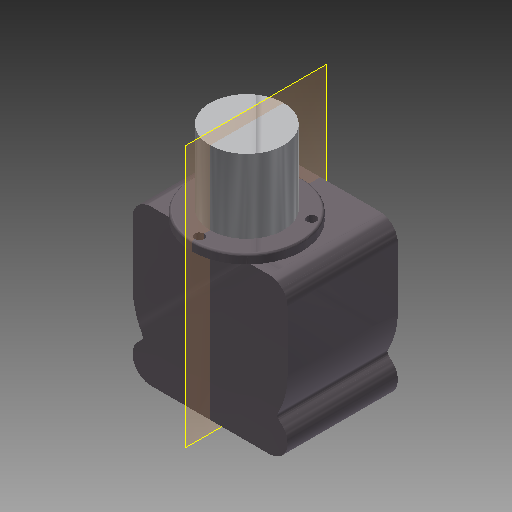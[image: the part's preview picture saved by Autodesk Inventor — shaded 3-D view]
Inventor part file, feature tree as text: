
AUTODESK INVENTOR PART (.ipt)
format: ipt  version: 2017 (Build 210142000, 142)  size: 190,976 bytes
history: native  units: in
note: dims shown in document units (in); Inventor stores cm internally (conversion verified against a paired STEP export)
features: sketch x5, extrude x4, fillet x3, reference x3, projected_geometry x2, hole x1
ambient origin geometry x8: Origin, YZ Plane, XZ Plane, XY Plane, X Axis, Y Axis, Z Axis, Center Point
bodies: Solid1 (feature_tree)
feature tree (18):
  extrude  "Extrusion1"  Depth=2.11in
  fillet  "Fillet1"  Radius=1.5in
  extrude  "Extrusion2"  Depth=0.5in
  fillet  "Fillet2"  Radius=0.5in
  extrude  "Extrusion3"  Depth=1.055in
  fillet  "Fillet3"  Radius=1.0in
  extrude  "Extrusion4"  Depth=1.5in
  hole  "Hole1"  [1 undecoded]
  sketch  "Sketch1"  dims[d0=2.11in d1=2.11in d2=1.5in d3=0.0in]
  sketch  "Sketch3"  dims[d4=0.25in d8=2.0in d9=0.5in]
  sketch  "Sketch4"  dims[d10=0.5in d12=1.055in d13=1.0in d14=0.0in]
  projected_geometry  "Projected Loop1"
  projected_geometry  "Projected Loop2"
  sketch  "Sketch5"  dims[d15=0.0625in d16=1.5in]
  sketch  "Sketch6"  dims[d17=0.25in d18=0.125in d19=0.0in d20=0.0312in d22=1.0in d23=0.0in d24=0.25in d25=0.129in d26=0.75in d27=0.225in d28=0.25in d29=0.5635in d30=0.25in d31=0.8108in]
  reference  "Reference1"
  reference  "Reference2"
  reference  "Reference3"
note: 1 required parameter value undecoded (feature->parameter linkage not recoverable at this tier; creation-order binding heuristic only, values carry confidence <= 0.55)
